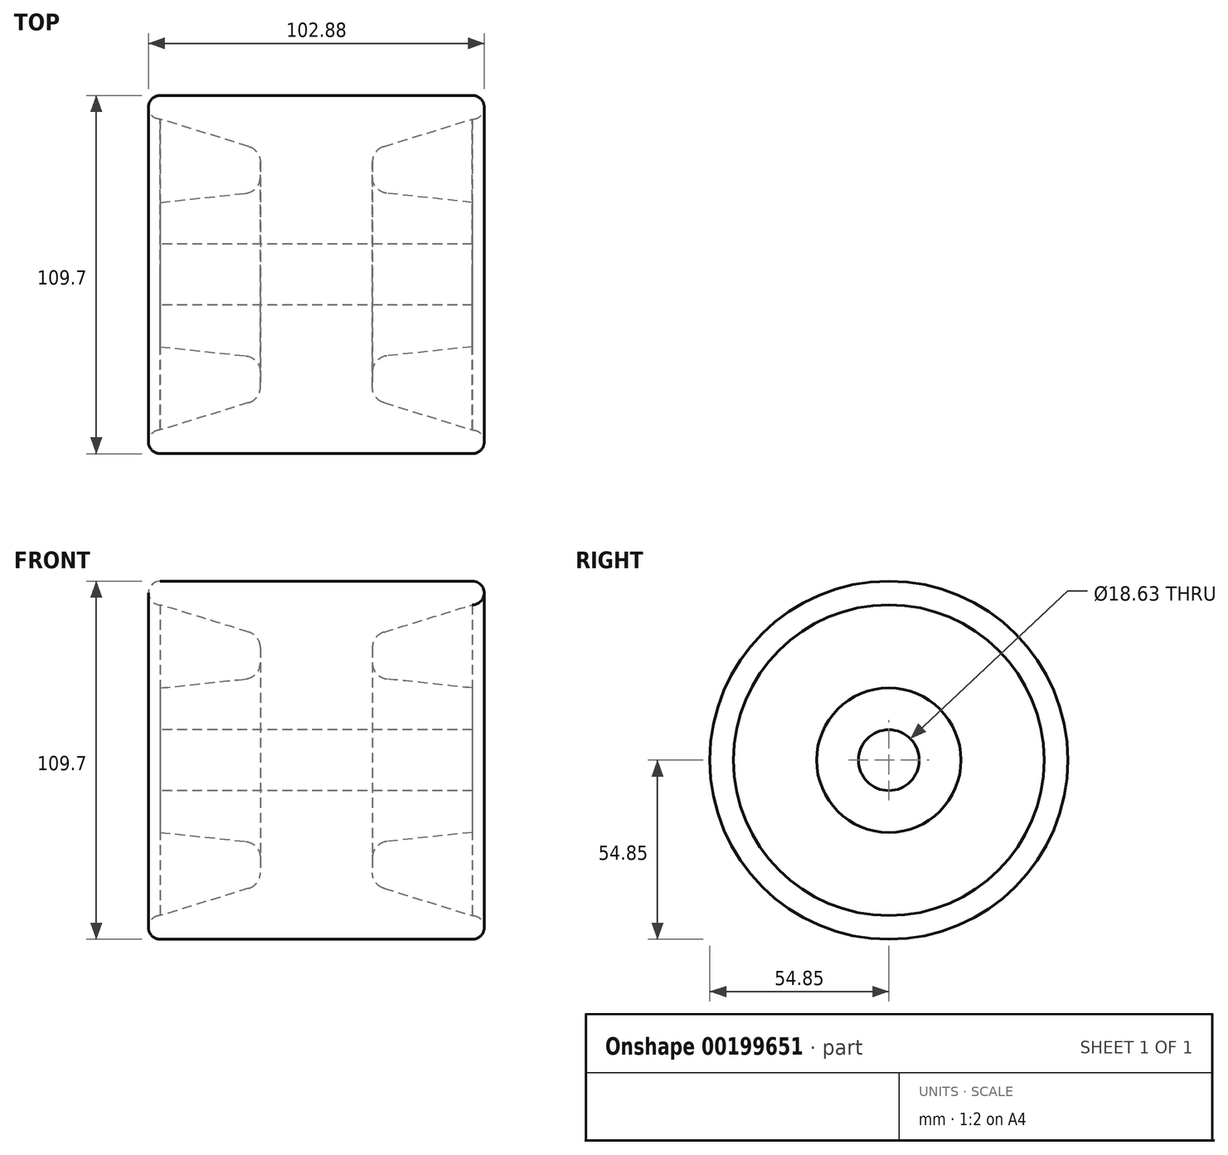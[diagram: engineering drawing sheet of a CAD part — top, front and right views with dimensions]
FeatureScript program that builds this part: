
annotation { "Feature Type Name" : "Feature", "Feature Type Description" : "" }
export const myFeature = defineFeature(function(context is Context, id is Id, definition is map)
    precondition{}
    {
        {
            var Q0;
            Q0=qCreatedBy(makeId("Top.planeOp"),FACE);
            var sketch = newSketch(context, id + "F0", { "sketchPlane" : qUnion([Q0])});
            skLineSegment(sketch, "E0", {"start": v(-47.8, -9.31) * mm, "end": v(0, -9.31) * mm});
            skLineSegment(sketch, "E1", {"start": v(0, -9.31) * mm, "end": v(0, -54.85) * mm});
            skLineSegment(sketch, "E2", {"start": v(0, -54.85) * mm, "end": v(-47.8, -54.85) * mm});
            skLineSegment(sketch, "E3", {"start": v(-47.8, -47.58) * mm, "end": v(-20.68, -39.22) * mm});
            skLineSegment(sketch, "E4", {"start": v(-17.16, -34.44) * mm, "end": v(-17.16, -29.85) * mm});
            skLineSegment(sketch, "E5", {"start": v(-21.63, -24.88) * mm, "end": v(-47.8, -22.1) * mm});
            skLineSegment(sketch, "E6", {"start": v(-47.8, -22.1) * mm, "end": v(-47.8, -9.31) * mm});
            skCircle(sketch, "E7", {"center": v(-47.8, -51.21) * mm, "radius": 3.63 * mm});
            skPoint(sketch, "E8.visualSharp", {"position": v(-17.16, -25.35) * mm});
            skArc(sketch, "E8.filletArc", {"start": v(-17.16, -29.85) * mm, "mid": v(-18.44, -26.5) * mm, "end": v(-21.63, -24.88) * mm});
            skPoint(sketch, "E9.visualSharp", {"position": v(-17.16, -38.13) * mm});
            skArc(sketch, "E9.filletArc", {"start": v(-20.68, -39.22) * mm, "mid": v(-18.13, -37.4) * mm, "end": v(-17.16, -34.44) * mm});
            skLineSegment(sketch, "E10.MirrorCS", {"start": v(17.16, -34.44) * mm, "end": v(17.16, -29.85) * mm});
            skArc(sketch, "E11.MirrorCS", {"start": v(20.68, -39.22) * mm, "mid": v(18.13, -37.4) * mm, "end": v(17.16, -34.44) * mm});
            skArc(sketch, "E12.MirrorCS", {"start": v(17.16, -29.85) * mm, "mid": v(18.44, -26.5) * mm, "end": v(21.63, -24.88) * mm});
            skLineSegment(sketch, "E13.MirrorCS", {"start": v(47.8, -9.31) * mm, "end": v(0, -9.31) * mm});
            skPoint(sketch, "E14.MirrorP", {"position": v(17.16, -38.13) * mm});
            skLineSegment(sketch, "E15.MirrorCS", {"start": v(0, -54.85) * mm, "end": v(47.8, -54.85) * mm});
            skPoint(sketch, "E16.MirrorP", {"position": v(17.16, -25.35) * mm});
            skLineSegment(sketch, "E17.MirrorCS", {"start": v(21.63, -24.88) * mm, "end": v(47.8, -22.1) * mm});
            skLineSegment(sketch, "E18.MirrorCS", {"start": v(47.8, -47.58) * mm, "end": v(20.68, -39.22) * mm});
            skCircle(sketch, "E19.MirrorC", {"center": v(47.8, -51.21) * mm, "radius": 3.63 * mm});
            skLineSegment(sketch, "E20.MirrorCS", {"start": v(47.8, -22.1) * mm, "end": v(47.8, -9.31) * mm});
            skLineSegment(sketch, "E21", {"start": v(-51.94, 0) * mm, "end": v(52.14, 0) * mm, "construction": true});
            skSolve(sketch);
        }
        {
            var Q0;
            Q0 = qSketchRegion(id + "F0", true);
            var Q1;
            Q1=sQuery(id+"F0.wireOp",EDGE,"E21");
            revolve(context, id + "F1", {"entities" : qUnion([Q0]), "axis" : qUnion([Q1]), "revolveType" : RevolveType.FULL});
        }
    });
